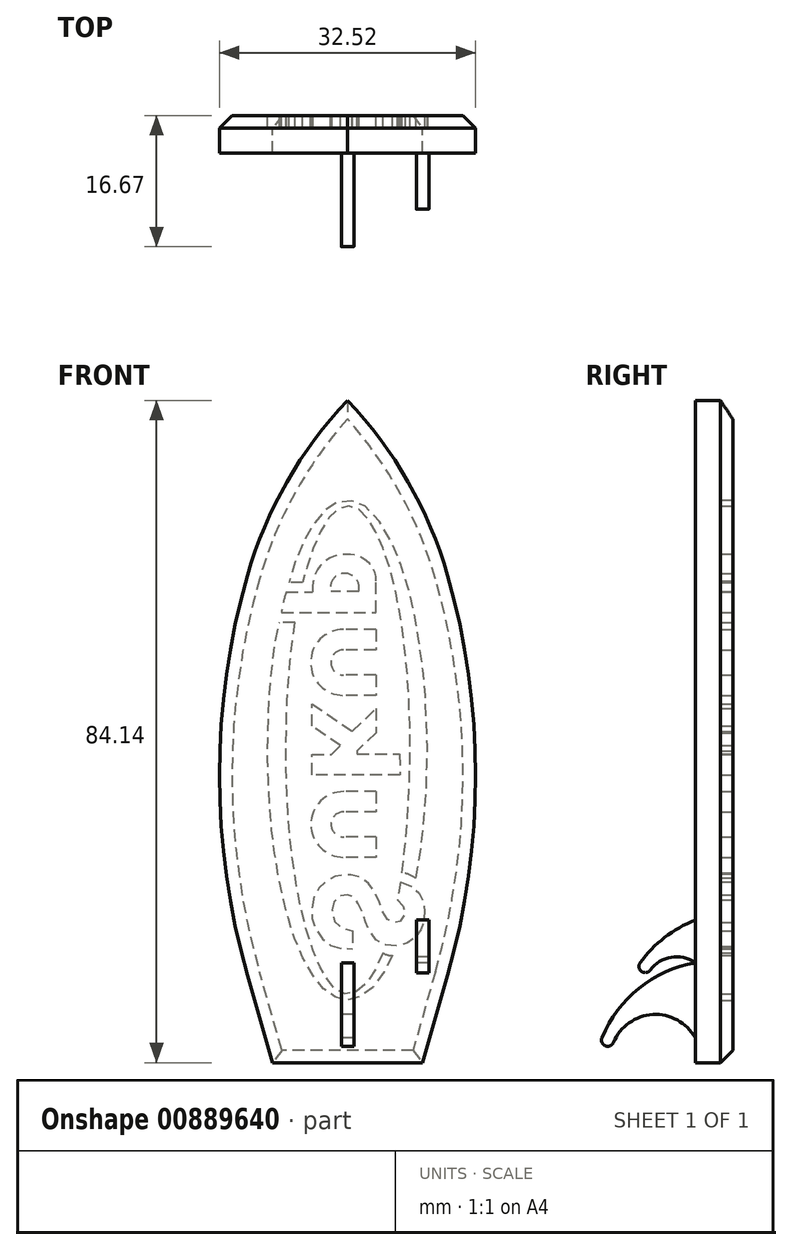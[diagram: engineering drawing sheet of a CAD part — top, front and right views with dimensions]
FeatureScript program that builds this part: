
annotation { "Feature Type Name" : "Feature", "Feature Type Description" : "" }
export const myFeature = defineFeature(function(context is Context, id is Id, definition is map)
    precondition{}
    {
        {
            var Q0;
            Q0=qCreatedBy(makeId("Front.planeOp"),FACE);
            var sketch = newSketch(context, id + "F0", { "sketchPlane" : qUnion([Q0])});
            skLineSegment(sketch, "E0", {"start": v(0, 0) * mm, "end": v(-9.53, -11.11) * mm, "construction": true});
            skLineSegment(sketch, "E1", {"start": v(-9.53, -11.11) * mm, "end": v(-12.7, 0) * mm});
            skLineSegment(sketch, "E2", {"start": v(0, 0) * mm, "end": v(9.53, -11.11) * mm, "construction": true});
            skLineSegment(sketch, "E3", {"start": v(9.53, -11.11) * mm, "end": v(12.7, 0) * mm});
            skLineSegment(sketch, "E4", {"start": v(-12.7, 0) * mm, "end": v(0, 0) * mm, "construction": true});
            skLineSegment(sketch, "E5", {"start": v(12.7, 0) * mm, "end": v(0, 0) * mm, "construction": true});
            skLineSegment(sketch, "E6", {"start": v(-9.53, -11.11) * mm, "end": v(0, -11.11) * mm});
            skLineSegment(sketch, "E7", {"start": v(0, -11.11) * mm, "end": v(0, 0) * mm, "construction": true});
            skLineSegment(sketch, "E8", {"start": v(0, -11.11) * mm, "end": v(9.53, -11.11) * mm});
            skArc(sketch, "E9", {"start": v(-12.7, 50.8) * mm, "mid": v(-16.26, 25.4) * mm, "end": v(-12.7, 0) * mm});
            skArc(sketch, "E10", {"start": v(12.7, 0) * mm, "mid": v(16.26, 25.4) * mm, "end": v(12.7, 50.8) * mm});
            skArc(sketch, "E11", {"start": v(0, 73.03) * mm, "mid": v(-7.7, 62.68) * mm, "end": v(-12.7, 50.8) * mm});
            skArc(sketch, "E12", {"start": v(12.7, 50.8) * mm, "mid": v(7.7, 62.68) * mm, "end": v(0, 73.03) * mm});
            skLineSegment(sketch, "E13", {"start": v(-12.7, 50.8) * mm, "end": v(0, 50.8) * mm, "construction": true});
            skLineSegment(sketch, "E14", {"start": v(0, 50.8) * mm, "end": v(0, 0) * mm, "construction": true});
            skLineSegment(sketch, "E15", {"start": v(12.7, 50.8) * mm, "end": v(0, 50.8) * mm, "construction": true});
            skSolve(sketch);
        }
        {
            var Q0;
            Q0 = qSketchRegion(id + "F0", true);
            extrude(context, id + "F1", {"entities" : qUnion([Q0]), "depth" : 4.76 * mm, "offsetDistance" : 25.4 * mm});
        }
        {
            var Q0;
            Q0=qCreatedBy(makeId("Right.planeOp"),FACE);
            var sketch = newSketch(context, id + "F2", { "sketchPlane" : qUnion([Q0])});
            skLineSegment(sketch, "E16", {"start": v(-4.76, 1.59) * mm, "end": v(-4.76, -7.94) * mm});
            skArc(sketch, "E17", {"start": v(-4.76, 1.59) * mm, "mid": v(-11.9, -1.67) * mm, "end": v(-16.6, -7.94) * mm});
            skArc(sketch, "E18", {"start": v(-4.76, -7.94) * mm, "mid": v(-10.14, -5) * mm, "end": v(-15.14, -8.55) * mm});
            skLineSegment(sketch, "E19", {"start": v(-16.6, -7.94) * mm, "end": v(-15.14, -8.55) * mm, "construction": true});
            skArc(sketch, "E20", {"start": v(-16.6, -7.94) * mm, "mid": v(-16.18, -8.98) * mm, "end": v(-15.14, -8.55) * mm});
            skSolve(sketch);
        }
        {
            var Q0;
            Q0 = qSketchRegion(id + "F2", true);
            extrude(context, id + "F3", {"entities" : qUnion([Q0]), "operationType" : NewBodyOperationType.ADD, "endBound" : BoundingType.SYMMETRIC, "depth" : 1.59 * mm, "offsetDistance" : 25.4 * mm});
        }
        {
            var Q0;
            Q0=qCreatedBy(makeId("Right.planeOp"),FACE);
            cPlane(context, id + "F4", {"entities" : qUnion([Q0]), "cplaneType" : CPlaneType.OFFSET, "offset" : 9.52 * mm, "width" : 152.4 * mm, "height" : 152.4 * mm});
        }
        {
            var Q0;
            Q0=qCreatedBy(id+"F4.planeOp",FACE);
            var sketch = newSketch(context, id + "F5", { "sketchPlane" : qUnion([Q0])});
            skLineSegment(sketch, "E21", {"start": v(-4.76, 7) * mm, "end": v(-4.76, 1.59) * mm});
            skArc(sketch, "E22", {"start": v(-4.76, 7) * mm, "mid": v(-8.64, 4.79) * mm, "end": v(-11.75, 1.59) * mm});
            skArc(sketch, "E23", {"start": v(-4.76, 1.59) * mm, "mid": v(-7.8, 2.3) * mm, "end": v(-10.47, 0.65) * mm});
            skLineSegment(sketch, "E24", {"start": v(-11.75, 1.59) * mm, "end": v(-10.47, 0.65) * mm, "construction": true});
            skArc(sketch, "E25", {"start": v(-11.75, 1.59) * mm, "mid": v(-11.58, 0.48) * mm, "end": v(-10.47, 0.65) * mm});
            skSolve(sketch);
        }
        {
            var Q0;
            Q0 = qSketchRegion(id + "F5", true);
            extrude(context, id + "F6", {"entities" : qUnion([Q0]), "operationType" : NewBodyOperationType.ADD, "endBound" : BoundingType.SYMMETRIC, "depth" : 1.59 * mm, "offsetDistance" : 25.4 * mm});
        }
        {
            var Q0;
            Q0=makeQuery(id+"F1.opExtrude","CAP_EDGE",EDGE,{"disambiguationData":[OSD([sQuery(id+"F0.wireOp",EDGE,"E9")])],"isStart":true});
            var Q1;
            Q1=makeQuery(id+"F1.opExtrude","CAP_EDGE",EDGE,{"disambiguationData":[OSD([sQuery(id+"F0.wireOp",EDGE,"E10")])],"isStart":true});
            var Q2;
            Q2=makeQuery(id+"F1.opExtrude","CAP_EDGE",EDGE,{"disambiguationData":[OSD([sQuery(id+"F0.wireOp",EDGE,"E6"),sQuery(id+"F0.wireOp",EDGE,"E8")])],"isStart":true});
            chamfer(context, id + "F7", {"entities" : qUnion([Q0, Q1, Q2]), "width" : 1.59 * mm, "tangentPropagation" : true});
        }
        {
            var Q0;
            Q0=makeQuery(id+"F1.opExtrude","CAP_FACE",FACE,{"disambiguationData":[OSD([sQuery(id+"F0.wireOp",EDGE,"E1"),sQuery(id+"F0.wireOp",EDGE,"E3"),sQuery(id+"F0.wireOp",EDGE,"E6"),sQuery(id+"F0.wireOp",EDGE,"E8"),sQuery(id+"F0.wireOp",EDGE,"E9"),sQuery(id+"F0.wireOp",EDGE,"E10"),sQuery(id+"F0.wireOp",EDGE,"E11"),sQuery(id+"F0.wireOp",EDGE,"E12")])],"isStart":true});
            var sketch = newSketch(context, id + "F8", { "sketchPlane" : qUnion([Q0])});
            skLineSegment(sketch, "E26", {"start": v(0, -3.17) * mm, "end": v(0, -9.52) * mm, "construction": true});
            skLineSegment(sketch, "E27", {"start": v(-6.67, 25.44) * mm, "end": v(4.5, 25.44) * mm});
            skLineSegment(sketch, "E28", {"start": v(4.5, 25.44) * mm, "end": v(4.5, 28.06) * mm});
            skLineSegment(sketch, "E29", {"start": v(4.5, 28.06) * mm, "end": v(2.03, 28.06) * mm});
            skLineSegment(sketch, "E30", {"start": v(2.03, 28.06) * mm, "end": v(0.9, 29.2) * mm});
            skLineSegment(sketch, "E31", {"start": v(0.9, 29.2) * mm, "end": v(4.5, 31.64) * mm});
            skLineSegment(sketch, "E32", {"start": v(4.5, 31.64) * mm, "end": v(4.5, 34.45) * mm});
            skLineSegment(sketch, "E33", {"start": v(4.5, 34.45) * mm, "end": v(-0.6, 31) * mm});
            skLineSegment(sketch, "E34", {"start": v(-0.6, 31) * mm, "end": v(-3.64, 33.86) * mm});
            skLineSegment(sketch, "E35", {"start": v(-3.64, 33.86) * mm, "end": v(-3.64, 30.8) * mm});
            skLineSegment(sketch, "E36", {"start": v(-3.64, 30.8) * mm, "end": v(-1.2, 28.5) * mm});
            skLineSegment(sketch, "E37", {"start": v(-1.2, 28.5) * mm, "end": v(-1.2, 28.12) * mm});
            skLineSegment(sketch, "E38", {"start": v(-1.2, 28.12) * mm, "end": v(-6.62, 28.12) * mm});
            skLineSegment(sketch, "E39", {"start": v(-6.62, 28.12) * mm, "end": v(-6.67, 25.44) * mm});
            skLineSegment(sketch, "E40", {"start": v(-3.64, 17.55) * mm, "end": v(0.47, 17.55) * mm});
            skLineSegment(sketch, "E41", {"start": v(-3.64, 17.55) * mm, "end": v(-3.64, 14.98) * mm});
            skLineSegment(sketch, "E42", {"start": v(-3.64, 14.98) * mm, "end": v(0.47, 14.98) * mm});
            skLineSegment(sketch, "E43", {"start": v(-3.64, 23.33) * mm, "end": v(0.47, 23.33) * mm});
            skLineSegment(sketch, "E44", {"start": v(-3.64, 23.33) * mm, "end": v(-3.64, 20.77) * mm});
            skLineSegment(sketch, "E45", {"start": v(-3.64, 20.77) * mm, "end": v(0.47, 20.77) * mm});
            skLineSegment(sketch, "E46", {"start": v(0.47, 20.77) * mm, "end": v(0.47, 23.33) * mm, "construction": true});
            skLineSegment(sketch, "E47", {"start": v(0.47, 14.98) * mm, "end": v(0.47, 17.55) * mm, "construction": true});
            skArc(sketch, "E48", {"start": v(0.47, 17.55) * mm, "mid": v(2.08, 19.16) * mm, "end": v(0.47, 20.77) * mm});
            skArc(sketch, "E49", {"start": v(0.47, 14.98) * mm, "mid": v(4.64, 19.16) * mm, "end": v(0.47, 23.33) * mm});
            skLineSegment(sketch, "E50", {"start": v(6.67, 44.83) * mm, "end": v(8.65, 44.83) * mm});
            skLineSegment(sketch, "E51", {"start": v(-3.6, 38.12) * mm, "end": v(0.5, 38.12) * mm});
            skLineSegment(sketch, "E52", {"start": v(-3.6, 38.12) * mm, "end": v(-3.6, 35.55) * mm});
            skLineSegment(sketch, "E53", {"start": v(-3.6, 35.55) * mm, "end": v(0.5, 35.55) * mm});
            skLineSegment(sketch, "E54", {"start": v(-3.6, 43.9) * mm, "end": v(0.5, 43.9) * mm});
            skLineSegment(sketch, "E55", {"start": v(-3.6, 43.9) * mm, "end": v(-3.6, 41.34) * mm});
            skLineSegment(sketch, "E56", {"start": v(-3.6, 41.34) * mm, "end": v(0.5, 41.34) * mm});
            skLineSegment(sketch, "E57", {"start": v(0.5, 41.34) * mm, "end": v(0.5, 43.9) * mm, "construction": true});
            skLineSegment(sketch, "E58", {"start": v(0.5, 35.55) * mm, "end": v(0.5, 38.12) * mm, "construction": true});
            skArc(sketch, "E59", {"start": v(0.5, 38.12) * mm, "mid": v(2.12, 39.73) * mm, "end": v(0.5, 41.34) * mm});
            skArc(sketch, "E60", {"start": v(0.5, 35.55) * mm, "mid": v(4.69, 39.73) * mm, "end": v(0.5, 43.9) * mm});
            skArc(sketch, "E61", {"start": v(-5.7, 2.51) * mm, "mid": v(-5.09, 2.57) * mm, "end": v(-4.52, 2.83) * mm});
            skArc(sketch, "E62", {"start": v(8.39, 46.1) * mm, "mid": v(8.15, 47.42) * mm, "end": v(7.78, 48.7) * mm});
            skLineSegment(sketch, "E63", {"start": v(8.39, 46.1) * mm, "end": v(-3.64, 46.1) * mm});
            skLineSegment(sketch, "E64", {"start": v(-3.64, 46.1) * mm, "end": v(-3.64, 50.1) * mm});
            skLineSegment(sketch, "E65", {"start": v(7.78, 48.7) * mm, "end": v(4.43, 48.7) * mm});
            skLineSegment(sketch, "E66", {"start": v(-1.42, 48.73) * mm, "end": v(2.11, 48.73) * mm});
            skArc(sketch, "E67", {"start": v(2.11, 48.73) * mm, "mid": v(0.35, 51.05) * mm, "end": v(-1.42, 48.73) * mm});
            skFitSpline(sketch, "E68", {"points": [v(-3.64, 50.1) * mm, v(-3.48, 51.11) * mm, v(-2.85, 52.19) * mm, v(-1.79, 53.04) * mm, v(-1, 53.36) * mm, v(0, 53.46) * mm, v(1.05, 53.39) * mm, v(1.94, 53.11) * mm, v(2.78, 52.65) * mm, v(3.51, 51.96) * mm, v(4.03, 51.11) * mm, v(4.36, 50.1) * mm, v(4.43, 48.7) * mm], "startDerivative": vector(0.9, 12.48) * mm, "endDerivative": vector(-0.03, -15.2) * mm});
            skFitSpline(sketch, "E69", {"points": [v(-8.67, 12.34) * mm, v(-7.55, 12.88) * mm, v(-6.92, 13.01) * mm], "startDerivative": vector(2.05, 1.1) * mm, "endDerivative": vector(1.42, 0.18) * mm});
            skLineSegment(sketch, "E70", {"start": v(5.7, 49.92) * mm, "end": v(7.42, 49.92) * mm});
            skLineSegment(sketch, "E71", {"start": v(-6.74, 11.88) * mm, "end": v(-6.33, 9.54) * mm});
            skLineSegment(sketch, "E72", {"start": v(-0.61, 5.63) * mm, "end": v(-0.61, 3.34) * mm});
            skFitSpline(sketch, "E73", {"points": [v(-6.33, 9.54) * mm, v(-6.68, 9.24) * mm, v(-7.06, 8.78) * mm, v(-7.26, 8.28) * mm, v(-7.25, 7.71) * mm, v(-6.99, 7.17) * mm, v(-6.7, 6.85) * mm, v(-6.36, 6.7) * mm, v(-6.07, 6.66) * mm, v(-5.7, 6.71) * mm, v(-5.34, 6.92) * mm, v(-5.1, 7.12) * mm, v(-4.8, 7.5) * mm, v(-4.37, 8.32) * mm, v(-4.06, 9.19) * mm, v(-3.76, 9.96) * mm, v(-3.38, 10.66) * mm, v(-2.9, 11.37) * mm, v(-2.44, 11.83) * mm, v(-1.7, 12.37) * mm, v(-1.03, 12.65) * mm, v(-0.5, 12.76) * mm, v(-0.04, 12.78) * mm, v(0.37, 12.77) * mm, v(1.05, 12.66) * mm, v(1.48, 12.56) * mm, v(1.97, 12.34) * mm, v(2.6, 12) * mm, v(3.25, 11.45) * mm, v(3.74, 10.9) * mm, v(4.13, 10.25) * mm, v(4.42, 9.43) * mm, v(4.53, 8.36) * mm, v(4.52, 7.47) * mm, v(4.38, 6.78) * mm, v(3.99, 5.8) * mm, v(3.36, 4.85) * mm, v(2.88, 4.31) * mm, v(2.1, 3.79) * mm, v(1.22, 3.5) * mm, v(0.36, 3.36) * mm, v(-0.61, 3.34) * mm], "startDerivative": vector(-16.84, -13.57) * mm, "endDerivative": vector(-33.73, 0.35) * mm});
            skFitSpline(sketch, "E74", {"points": [v(-6.74, 11.88) * mm, v(-7.86, 11.45) * mm, v(-8.57, 11) * mm, v(-9.05, 10.5) * mm, v(-9.53, 9.73) * mm, v(-9.73, 9) * mm, v(-9.8, 8.23) * mm, v(-9.8, 7.59) * mm, v(-9.73, 6.99) * mm, v(-9.54, 6.34) * mm, v(-9.2, 5.6) * mm, v(-8.75, 5) * mm, v(-8.26, 4.54) * mm, v(-7.68, 4.15) * mm, v(-6.82, 3.8) * mm, v(-5.93, 3.68) * mm, v(-4.8, 3.85) * mm, v(-3.98, 4.24) * mm, v(-3.3, 4.83) * mm, v(-2.75, 5.67) * mm, v(-2.42, 6.42) * mm, v(-2.2, 7.13) * mm, v(-1.96, 7.84) * mm, v(-1.6, 8.6) * mm, v(-1.3, 9.2) * mm, v(-0.95, 9.71) * mm, v(-0.8, 9.91) * mm, v(-0.62, 10.05) * mm, v(-0.28, 10.2) * mm, v(0.3, 10.21) * mm, v(0.84, 10.1) * mm, v(1.28, 9.83) * mm, v(1.63, 9.45) * mm, v(1.8, 9.07) * mm, v(1.9, 8.73) * mm, v(1.93, 7.67) * mm, v(1.65, 6.8) * mm, v(1.22, 6.32) * mm, v(0.45, 5.91) * mm, v(-0.61, 5.63) * mm], "startDerivative": vector(-39.09, -9.4) * mm, "endDerivative": vector(-38.27, -5.82) * mm});
            skFitSpline(sketch, "E75", {"points": [v(-4.52, 2.83) * mm, v(-3.6, 0.86) * mm, v(-2.74, -0.6) * mm, v(-1.85, -1.59) * mm, v(-1.02, -2.16) * mm, v(-0.2, -2.41) * mm, v(0.76, -2.22) * mm, v(1.57, -1.73) * mm, v(2.15, -1.14) * mm, v(2.62, -0.47) * mm, v(3.35, 0.77) * mm, v(4.03, 2.24) * mm, v(5.04, 5.05) * mm, v(5.84, 8.18) * mm, v(6.6, 12.04) * mm, v(7.1, 15.56) * mm, v(7.43, 19.12) * mm, v(7.62, 21.77) * mm, v(7.76, 24.95) * mm, v(7.82, 29.27) * mm, v(7.75, 32.11) * mm, v(7.68, 34.92) * mm, v(7.49, 37.64) * mm, v(7.28, 40.05) * mm, v(6.95, 42.66) * mm, v(6.67, 44.83) * mm], "startDerivative": vector(22.8, -50.47) * mm, "endDerivative": vector(-6.4, 52.2) * mm});
            skFitSpline(sketch, "E76", {"points": [v(-5.7, 2.51) * mm, v(-5.03, 1.1) * mm, v(-3.85, -0.78) * mm, v(-2.92, -1.84) * mm, v(-1.94, -2.56) * mm, v(-0.82, -3.03) * mm, v(0, -3.17) * mm, v(0.8, -3.05) * mm, v(1.5, -2.8) * mm, v(2.29, -2.36) * mm, v(3.22, -1.53) * mm, v(4.13, -0.44) * mm, v(5.15, 1.23) * mm, v(6.23, 3.42) * mm, v(6.93, 5.28) * mm, v(7.61, 7.53) * mm, v(8.1, 9.4) * mm, v(8.66, 11.98) * mm, v(9.15, 14.83) * mm, v(9.56, 17.63) * mm, v(9.82, 20.71) * mm, v(10.02, 24.2) * mm, v(10.11, 26.32) * mm, v(10.15, 28.58) * mm, v(10.1, 30.74) * mm, v(10.04, 33.2) * mm, v(9.85, 36.2) * mm, v(9.56, 39.35) * mm, v(9.22, 42.04) * mm, v(8.65, 44.83) * mm], "startDerivative": vector(19.7, -43.91) * mm, "endDerivative": vector(-15.06, 68.16) * mm});
            skFitSpline(sketch, "E77", {"points": [v(-6.92, 13.01) * mm, v(-7.31, 16.43) * mm, v(-7.66, 20.3) * mm, v(-7.85, 24.27) * mm, v(-7.96, 28.1) * mm, v(-7.9, 32.36) * mm, v(-7.72, 36.34) * mm, v(-7.34, 41) * mm, v(-6.75, 45.3) * mm, v(-5.89, 49.8) * mm, v(-4.77, 53.6) * mm, v(-3.84, 55.84) * mm, v(-3.11, 57.22) * mm, v(-2.4, 58.24) * mm, v(-1.62, 59) * mm, v(-0.9, 59.46) * mm, v(-0.23, 59.59) * mm, v(0.7, 59.47) * mm, v(1.38, 59.1) * mm, v(2.03, 58.5) * mm, v(2.84, 57.4) * mm, v(3.77, 55.7) * mm, v(4.6, 53.54) * mm, v(5.29, 51.36) * mm, v(5.7, 49.92) * mm], "startDerivative": vector(-7.9, 66.37) * mm, "endDerivative": vector(11.42, -40.6) * mm});
            skPoint(sketch, "E78.9.internal.snap0", {"position": v(-10.15, 28.58) * mm});
            skFitSpline(sketch, "E78", {"points": [v(-8.67, 12.34) * mm, v(-9.19, 15.12) * mm, v(-9.45, 17.11) * mm, v(-9.64, 18.92) * mm, v(-9.78, 20.37) * mm, v(-9.91, 22.02) * mm, v(-10.02, 23.92) * mm, v(-10.07, 25.55) * mm, v(-10.08, 27.5) * mm, v(-10.15, 28.96) * mm, v(-10.08, 31.1) * mm, v(-10, 33.08) * mm, v(-9.83, 36.35) * mm, v(-9.6, 38.7) * mm, v(-9.09, 42.45) * mm, v(-8.6, 45.46) * mm, v(-8.05, 47.92) * mm, v(-7.46, 50.07) * mm, v(-6.67, 52.41) * mm, v(-6.13, 53.8) * mm, v(-5.01, 56.22) * mm, v(-3.83, 57.98) * mm, v(-2.51, 59.33) * mm, v(-1.76, 59.85) * mm, v(-1, 60.18) * mm, v(-0.34, 60.27) * mm, v(0.24, 60.28) * mm, v(1.22, 60.1) * mm, v(1.84, 59.8) * mm, v(2.74, 59.15) * mm, v(3.32, 58.56) * mm, v(3.8, 58) * mm, v(4.72, 56.66) * mm, v(5.64, 54.97) * mm, v(6.33, 53.38) * mm, v(7.07, 51.29) * mm, v(7.42, 49.92) * mm], "startDerivative": vector(-15.93, 81.22) * mm, "endDerivative": vector(11.3, -50.9) * mm});
            skSolve(sketch);
        }
        {
            var Q0;
            Q0 = qSketchRegion(id + "F8", true);
            extrude(context, id + "F9", {"entities" : qUnion([Q0]), "operationType" : NewBodyOperationType.REMOVE, "oppositeDirection" : true, "depth" : 1.59 * mm, "offsetDistance" : 25.4 * mm});
        }
    });
